# Revit family: Bath-Drain-Waterworks-Universal-Pop_up
name_source: partatom
category: Pipe Accessories
revit_build: Autodesk Revit MEP 2014 (Build: 20140709_2115(x64)
units: mm (PartAtom-declared; Revit-internal decimal feet)

## types (19) — shared parameters
Alt Finish = Metal - Waterworks - Unfinished
Assembly Code = D2010
Certification IAPMO = Yes
Certification State of MA = Yes
Certification cUPC = Yes
Code Compliance = Code # FDWO51: IAPMO
Default Elevation = 0' - 0"
Drain Hole Diameter = 0' - 2"
Horizontal Spread Maximum = 0' - 11 3/4"
Horizontal Spread Minimum = 0' - 6"
Keynote = 22 40 00
Length = 0' - 4"
Manufacturer = Waterworks
Model = UNWO51
Outlet Connection Size = 0' - 1 1/2"
Outlet Connection Type = Outlet - TallPiece
Product Documentation Link = http://assets.waterworks.com
Product Page URL = http://www.waterworks.com
URL = http://www.waterworks.com
Version = 2014 - v1.0a
Vertical Spread Maximum = 1' - 8"
Vertical Spread Minimum = 0' - 6 1/2"
Warranty = http://www.waterworks.com
‌Installation Requirements or Notes = For use with Waterworks Belevedere, Cambridge, Claremont, Minna, Durham, and Classic bathtubs

## per-type parameters (varying)
| type | Constraint | Description | Finish | Model SKU | Product Name |
| Burnished Nickel | 1 | Universal Pop-up Waste and Overflow Drain in Burnished Nickel | Metal - Waterworks - Burnished Nickel | 26-98706-79860 | Universal Pop-up Waste and Overflow Drain in Burnished Nickel |
| Carbon | 2 | Universal Pop-up Waste and Overflow Drain in Carbon | Metal - Waterworks - Carbon | 26-40358-18803 | Universal Pop-up Waste and Overflow Drain in Carbon |
| Graphite | 3 | Universal Pop-up Waste and Overflow Drain in Graphite | Metal - Waterworks - Graphite | 26-30897-59789 | Universal Pop-up Waste and Overflow Drain in Graphite |
| Shiny Copper | 4 | Universal Pop-up Waste and Overflow Drain in Shiny Copper | Metal - Waterworks - Shiny Copper | 26-07645-93617 | Universal Pop-up Waste and Overflow Drain in Shiny Copper |
| Antique Brass | 5 | Universal Pop-up Waste and Overflow Drain in Antique Brass | Metal - Waterworks - Antique Brass | 26-82316-78115 | Universal Pop-up Waste and Overflow Drain in Antique Brass |
| Antique Copper | 6 | Universal Pop-up Waste and Overflow Drain in Antique Copper | Metal - Waterworks - Antique Copper | 26-79991-92866 | Universal Pop-up Waste and Overflow Drain in Antique Copper |
| Architectural Bronze | 7 | Universal Pop-up Waste and Overflow Drain in Architectural Bronze | Metal - Waterworks - Architectural Bronze | 26-48789-97497 | Universal Pop-up Waste and Overflow Drain in Architectural Bronze |
| Burnished Brass | 8 | Universal Pop-up Waste and Overflow Drain in Burnished Brass | Metal - Waterworks - Burnished Brass | 26-61680-01258 | Universal Pop-up Waste and Overflow Drain in Burnished Brass |
| Chrome | 9 | Universal Pop-up Waste and Overflow Drain in Chrome | Metal - Waterworks - Chrome | 26-76104-28439 | Universal Pop-up Waste and Overflow Drain in Chrome |
| Gold | 10 | Universal Pop-up Waste and Overflow Drain in Gold | Metal - Waterworks - Gold | 26-85035-71009 | Universal Pop-up Waste and Overflow Drain in Gold |
| Matte Chrome | 11 | Universal Pop-up Waste and Overflow Drain in Matte Chrome | Metal - Waterworks - Matte Chrome | 26-63269-59968 | Universal Pop-up Waste and Overflow Drain in Matte Chrome |
| Matte Gold | 12 | Universal Pop-up Waste and Overflow Drain in Matte Gold | Metal - Waterworks - Matte Gold | 26-53766-40042 | Universal Pop-up Waste and Overflow Drain in Matte Gold |
| Matte Nickel | 13 | Universal Pop-up Waste and Overflow Drain in Matte Nickel | Metal - Waterworks - Matte Nickel | 26-13716-26324 | Universal Pop-up Waste and Overflow Drain in Matte Nickel |
| Nickel | 14 | Universal Pop-up Waste and Overflow Drain in Nickel | Metal - Waterworks - Nickel | 26-23260-40483 | Universal Pop-up Waste and Overflow Drain in Nickel |
| Pewter | 15 | Universal Pop-up Waste and Overflow Drain in Pewter | Metal - Waterworks - Pewter | 26-36075-85449 | Universal Pop-up Waste and Overflow Drain in Pewter |
| Sovereign | 16 | Universal Pop-up Waste and Overflow Drain in Sovereign | Metal - Waterworks - Sovereign | 26-71091-33219 | Universal Pop-up Waste and Overflow Drain in Sovereign |
| Unlacquered Brass | 17 | Universal Pop-up Waste and Overflow Drain in Unlacquered Brass | Metal - Waterworks - Unlacquered Brass | 26-39693-65746 | Universal Pop-up Waste and Overflow Drain in Unlacquered Brass |
| Vintage Brass | 18 | Universal Pop-up Waste and Overflow Drain in Vintage Brass | Metal - Waterworks - Vintage Brass | 26-38066-10815 | Universal Pop-up Waste and Overflow Drain in Vintage Brass |
| White | 19 | Universal Pop-up Waste and Overflow Drain in White | Metal - Waterworks - White | 26-16703-01157 | Universal Pop-up Waste and Overflow Drain in White |

## geometry (parser evidence)
native form markers: Sweep x4
no freeform markers — native parametric forms only
